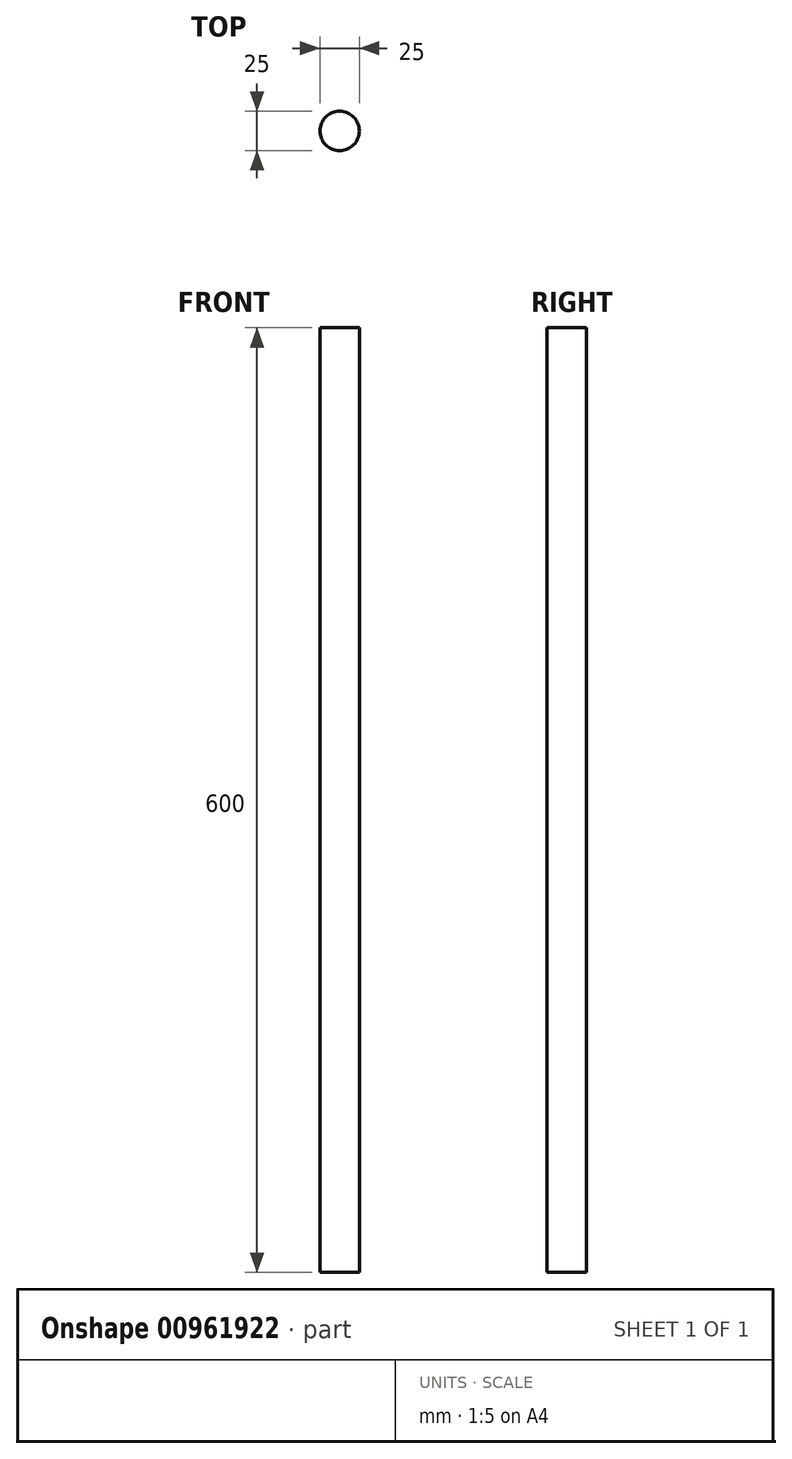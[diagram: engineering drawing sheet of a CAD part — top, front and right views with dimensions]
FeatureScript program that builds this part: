
annotation { "Feature Type Name" : "Feature", "Feature Type Description" : "" }
export const myFeature = defineFeature(function(context is Context, id is Id, definition is map)
    precondition{}
    {
        {
            var Q0;
            Q0=qCreatedBy(makeId("Top.planeOp"),FACE);
            var sketch = newSketch(context, id + "F0", { "sketchPlane" : qUnion([Q0])});
            skCircle(sketch, "E0", {"center": v(0, 0) * mm, "radius": 12.5 * mm});
            skSolve(sketch);
        }
        {
            var Q0;
            Q0=makeQuery(id+"F0.imprint","IMPRINT",FACE,{"disambiguationData":[TD([[makeQuery(id+"F0.imprint","IMPRINT",EDGE,{"derivedFrom":sQuery(id+"F0.wireOp",EDGE,"E0")}),1.0]])]});
            var Q1;
            Q1=sQuery(id+"F0.wireOp",EDGE,"E0");
            extrude(context, id + "F1", {"entities" : qUnion([Q0]), "surfaceEntities" : qUnion([Q1]), "oppositeDirection" : true, "depth" : 600 * mm, "offsetDistance" : 25 * mm});
        }
    });
